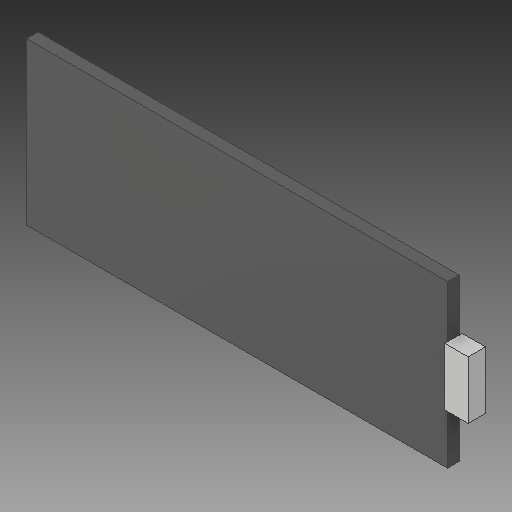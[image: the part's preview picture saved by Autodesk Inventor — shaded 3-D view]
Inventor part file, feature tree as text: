
AUTODESK INVENTOR PART (.ipt)
format: ipt  version: 2018 (Build 220112000, 112)  size: 897,024 bytes
history: native  units: in
note: dims shown in document units (in); Inventor stores cm internally (conversion verified against a paired STEP export)
features: sketch x7, other x5
ambient origin geometry x8: Origin, YZ Plane, XZ Plane, XY Plane, X Axis, Y Axis, Z Axis, Center Point
bodies: Solid1 (feature_tree), Solid2 (feature_tree), Solid3 (feature_tree)
feature tree (12):
  other  "Solar_panel1.ipt"
  other  "Solid1::Solar_panel1.ipt"
  other  "Solid2::Solar_panel1.ipt"
  other  "Solid3::Solar_panel1.ipt"
  other  "TaggingFeature1"
  sketch  "Sketch1"  dims[d0=0.3937in]
  sketch  "Sketch2"
  sketch  "Sketch3"
  sketch  "Sketch4"
  sketch  "Sketch5"
  sketch  "Sketch6"
  sketch  "Sketch7"
